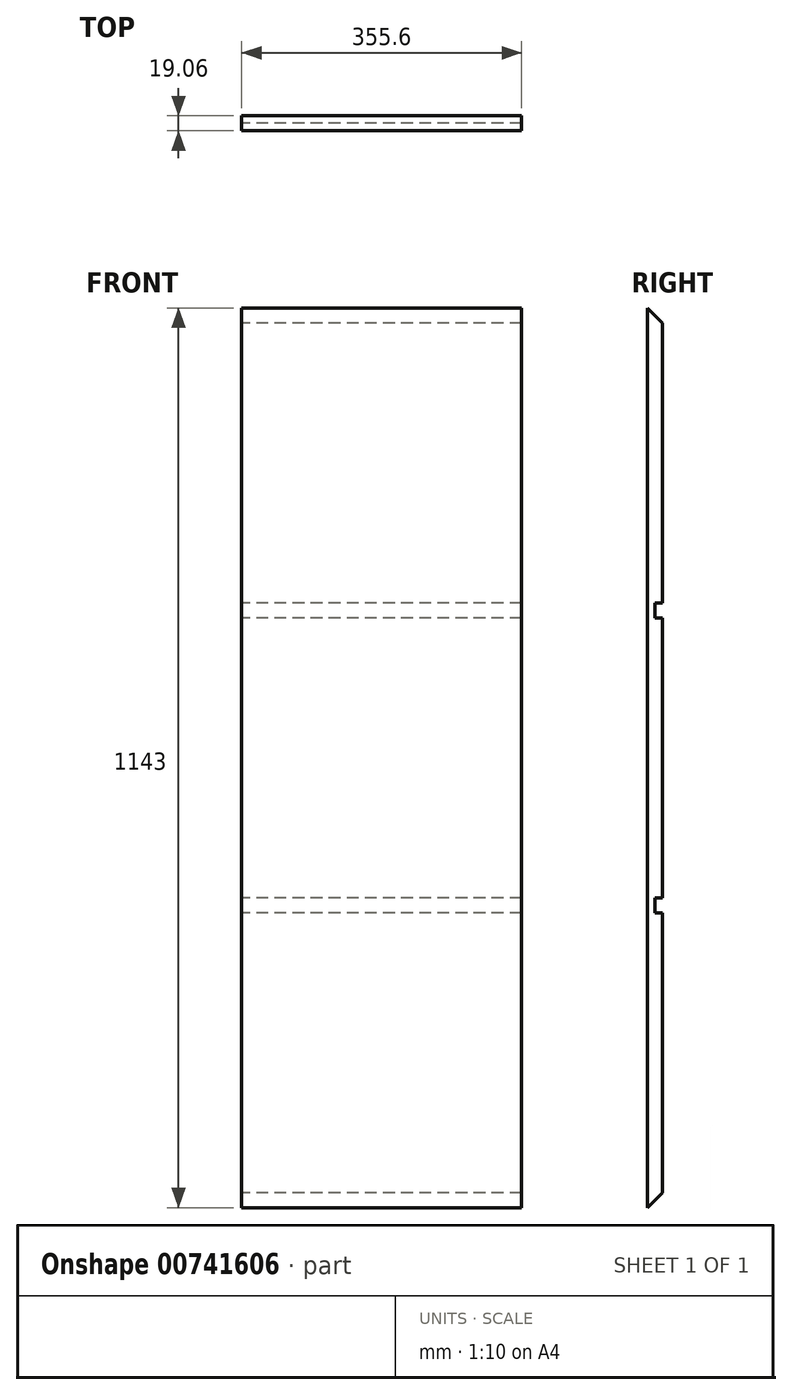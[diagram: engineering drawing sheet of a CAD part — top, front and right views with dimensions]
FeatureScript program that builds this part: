
annotation { "Feature Type Name" : "Feature", "Feature Type Description" : "" }
export const myFeature = defineFeature(function(context is Context, id is Id, definition is map)
    precondition{}
    {
        {
            var Q0;
            Q0=qCreatedBy(makeId("Right.planeOp"),FACE);
            var sketch = newSketch(context, id + "F0", { "sketchPlane" : qUnion([Q0])});
            skLineSegment(sketch, "E0.left", {"start": v(-9.52, 571.5) * mm, "end": v(-9.53, -571.5) * mm});
            skLineSegment(sketch, "E0.right", {"start": v(9.53, 552.45) * mm, "end": v(9.53, 196.85) * mm});
            skPoint(sketch, "E0.middle", {"position": v(0, 0) * mm});
            skLineSegment(sketch, "E1", {"start": v(-9.53, 571.5) * mm, "end": v(9.53, 552.45) * mm});
            skPoint(sketch, "E2.orphan", {"position": v(9.53, 571.5) * mm});
            skLineSegment(sketch, "E3", {"start": v(-9.52, -571.5) * mm, "end": v(9.52, -552.45) * mm});
            skPoint(sketch, "E0.top.end.orphan", {"position": v(9.52, -571.5) * mm});
            skLineSegment(sketch, "E4", {"start": v(9.52, -552.45) * mm, "end": v(9.52, -196.85) * mm});
            skLineSegment(sketch, "E5.bottom", {"start": v(9.52, -196.85) * mm, "end": v(0, -196.85) * mm});
            skLineSegment(sketch, "E5.top", {"start": v(9.52, -177.8) * mm, "end": v(0, -177.8) * mm});
            skLineSegment(sketch, "E5.right", {"start": v(0, -196.85) * mm, "end": v(0, -177.8) * mm});
            skLineSegment(sketch, "E6", {"start": v(9.52, -177.8) * mm, "end": v(9.53, 177.8) * mm});
            skLineSegment(sketch, "E7.bottom", {"start": v(9.53, 177.8) * mm, "end": v(0, 177.8) * mm});
            skLineSegment(sketch, "E7.top", {"start": v(9.53, 196.85) * mm, "end": v(0, 196.85) * mm});
            skLineSegment(sketch, "E7.right", {"start": v(0, 177.8) * mm, "end": v(0, 196.85) * mm});
            skLineSegment(sketch, "E8.trimOffspring", {"start": v(9.53, 177.8) * mm, "end": v(9.52, -177.8) * mm});
            skSolve(sketch);
        }
        {
            var Q0;
            Q0 = qSketchRegion(id + "F0", true);
            extrude(context, id + "F1", {"entities" : qUnion([Q0]), "depth" : 355.6 * mm, "offsetDistance" : 25.4 * mm});
        }
    });
